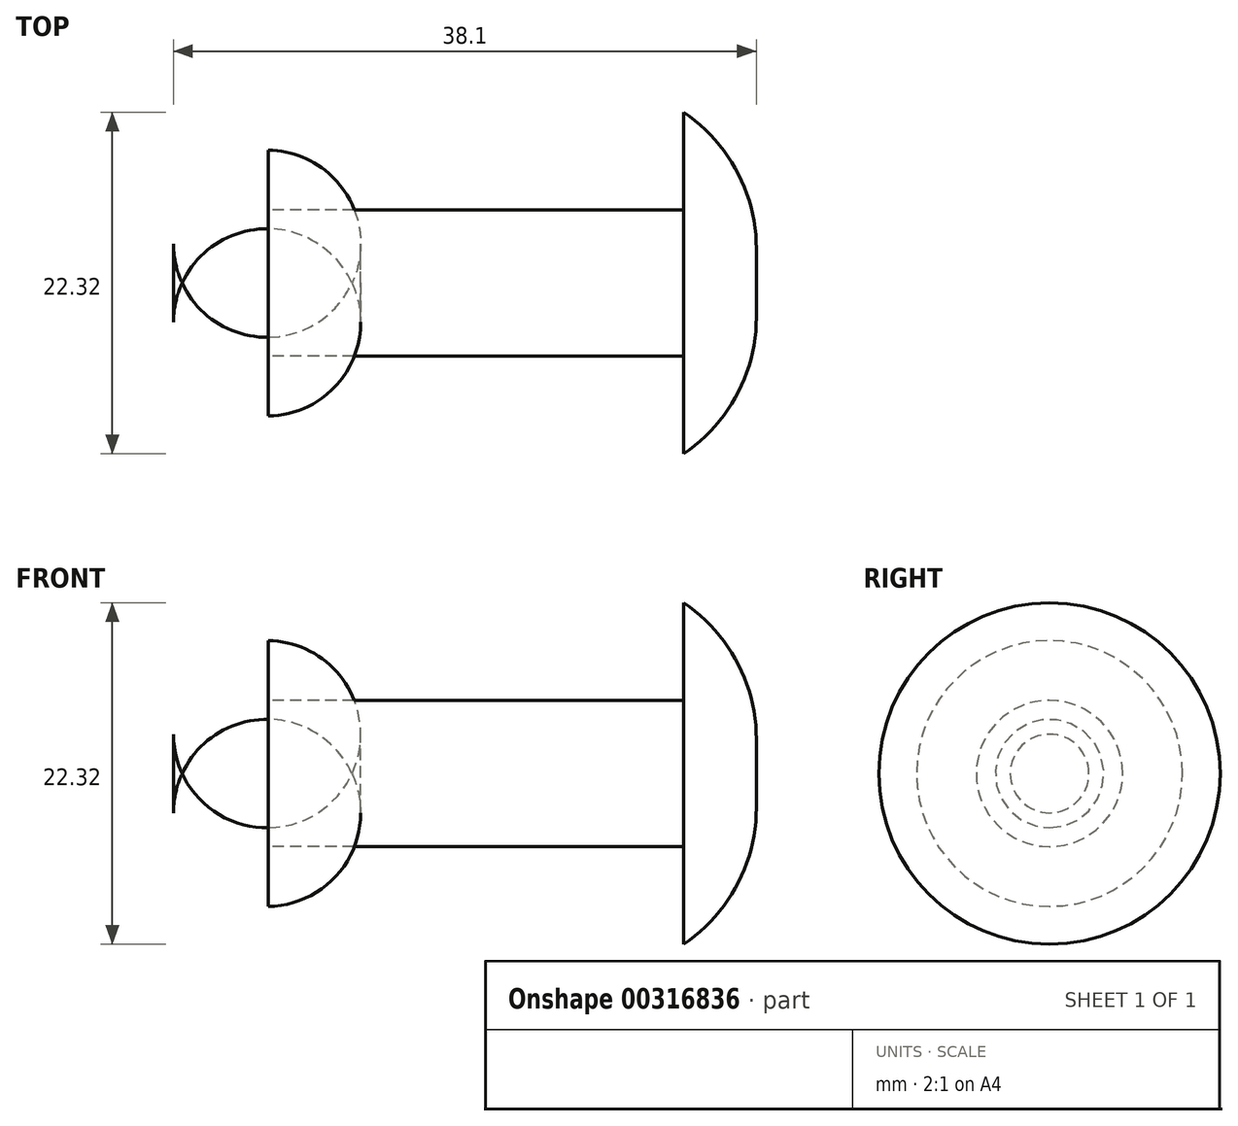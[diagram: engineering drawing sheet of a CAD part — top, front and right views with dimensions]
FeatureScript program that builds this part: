
annotation { "Feature Type Name" : "Feature", "Feature Type Description" : "" }
export const myFeature = defineFeature(function(context is Context, id is Id, definition is map)
    precondition{}
    {
        {
            var Q0;
            Q0=qCreatedBy(makeId("Front.planeOp"),FACE);
            var sketch = newSketch(context, id + "F0", { "sketchPlane" : qUnion([Q0])});
            skLineSegment(sketch, "E0", {"start": v(0, 0) * mm, "end": v(38.1, 0) * mm});
            skLineSegment(sketch, "E1", {"start": v(33.34, 11.16) * mm, "end": v(33.34, 4.78) * mm});
            skLineSegment(sketch, "E2", {"start": v(33.34, 4.78) * mm, "end": v(6.2, 4.78) * mm});
            skLineSegment(sketch, "E3", {"start": v(0, 0) * mm, "end": v(0, 2.57) * mm});
            skLineSegment(sketch, "E4", {"start": v(6.2, 4.78) * mm, "end": v(6.2, 8.69) * mm});
            skArc(sketch, "E5", {"start": v(6.2, 8.69) * mm, "mid": v(1.82, 6.93) * mm, "end": v(0, 2.57) * mm});
            skLineSegment(sketch, "E6", {"start": v(38.1, 0) * mm, "end": v(38.1, 2.25) * mm});
            skArc(sketch, "E7", {"start": v(38.1, 2.25) * mm, "mid": v(36.83, 7.3) * mm, "end": v(33.34, 11.16) * mm});
            skSolve(sketch);
        }
        {
            var Q0;
            Q0=makeQuery(id+"F0.imprint","IMPRINT",FACE,{"disambiguationData":[TD([[makeQuery(id+"F0.imprint","IMPRINT",EDGE,{"derivedFrom":sQuery(id+"F0.wireOp",EDGE,"E0")}),1.0]])]});
            var Q1;
            Q1=sQuery(id+"F0.wireOp",EDGE,"E0");
            revolve(context, id + "F1", {"entities" : qUnion([Q0]), "axis" : qUnion([Q1]), "revolveType" : RevolveType.FULL});
        }
    });
